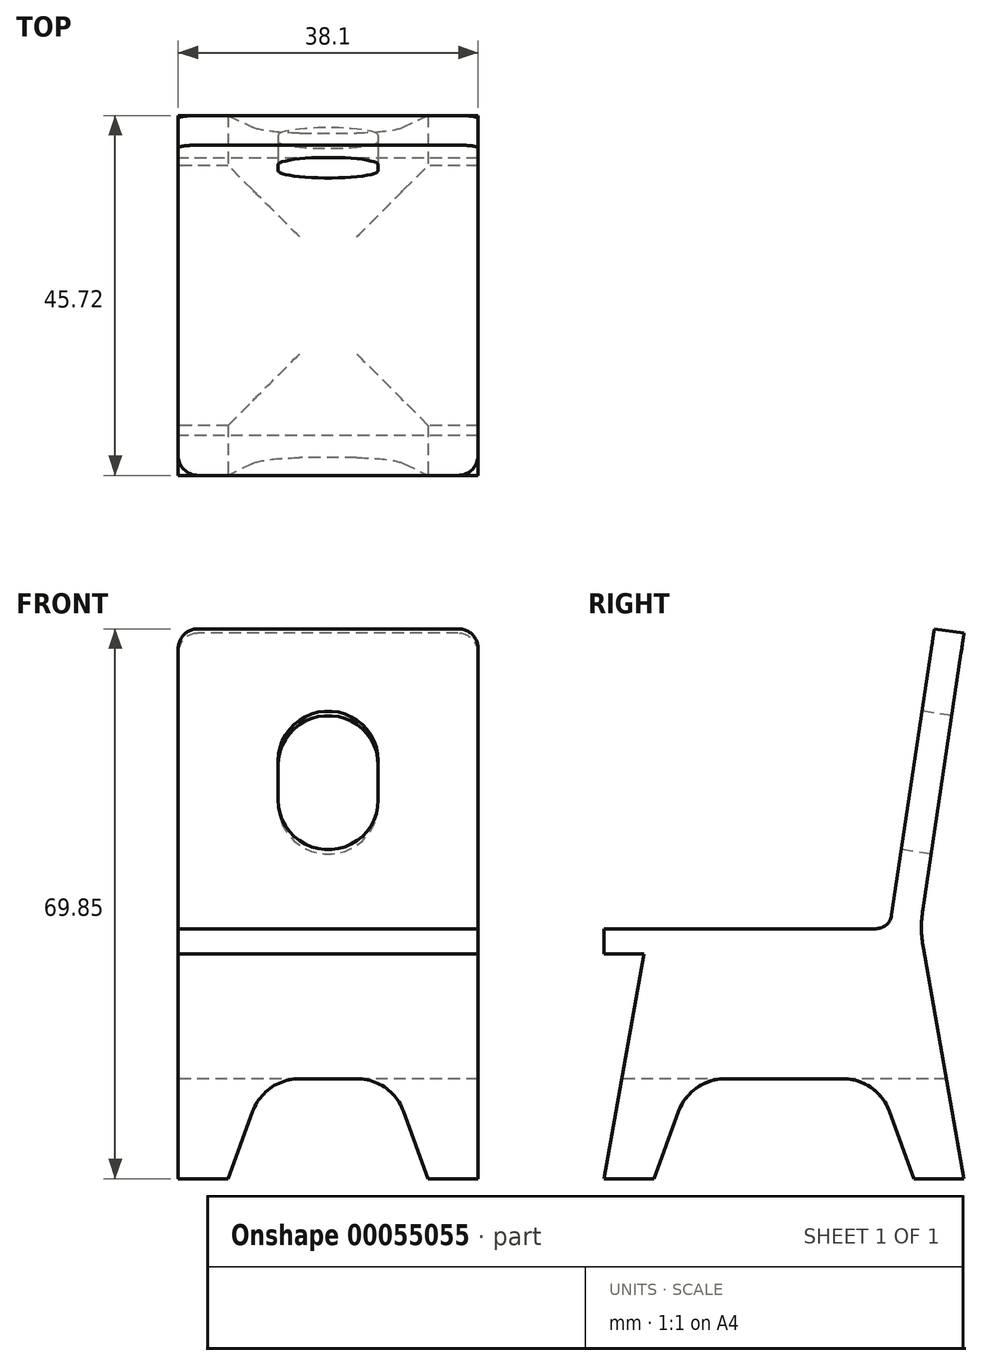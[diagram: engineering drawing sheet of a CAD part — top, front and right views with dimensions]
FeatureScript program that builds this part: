
annotation { "Feature Type Name" : "Feature", "Feature Type Description" : "" }
export const myFeature = defineFeature(function(context is Context, id is Id, definition is map)
    precondition{}
    {
        {
            var Q0;
            Q0=qCreatedBy(makeId("Right.planeOp"),FACE);
            var sketch = newSketch(context, id + "F0", { "sketchPlane" : qUnion([Q0])});
            skLineSegment(sketch, "E0", {"start": v(0.37, 2.45) * mm, "end": v(5.6, 37.54) * mm});
            skLineSegment(sketch, "E1", {"start": v(5.6, 37.54) * mm, "end": v(1.83, 38.1) * mm});
            skLineSegment(sketch, "E2", {"start": v(1.83, 38.1) * mm, "end": v(-3.6, 1.73) * mm});
            skLineSegment(sketch, "E3", {"start": v(-5.6, 0) * mm, "end": v(-40.12, 0) * mm});
            skLineSegment(sketch, "E4", {"start": v(-40.12, 0) * mm, "end": v(-40.12, -3.18) * mm});
            skLineSegment(sketch, "E5", {"start": v(-40.12, -3.18) * mm, "end": v(-35.08, -3.18) * mm});
            skLineSegment(sketch, "E6", {"start": v(-35.08, -3.18) * mm, "end": v(-40.12, -31.75) * mm});
            skLineSegment(sketch, "E7", {"start": v(-40.12, -31.75) * mm, "end": v(-33.77, -31.75) * mm});
            skLineSegment(sketch, "E8", {"start": v(-33.77, -31.75) * mm, "end": v(-30.67, -23.23) * mm});
            skLineSegment(sketch, "E9", {"start": v(-24.7, -19.05) * mm, "end": v(-9.82, -19.05) * mm});
            skLineSegment(sketch, "E10", {"start": v(-3.85, -23.23) * mm, "end": v(-0.75, -31.75) * mm});
            skLineSegment(sketch, "E11", {"start": v(5.6, -31.75) * mm, "end": v(0.43, -2.44) * mm});
            skLineSegment(sketch, "E12", {"start": v(-3.85, 0) * mm, "end": v(-3.85, 44.6) * mm, "construction": true});
            skLineSegment(sketch, "E13", {"start": v(-40.12, -3.18) * mm, "end": v(-40.12, -31.75) * mm, "construction": true});
            skLineSegment(sketch, "E14", {"start": v(-0.75, -31.75) * mm, "end": v(5.6, -31.75) * mm});
            skLineSegment(sketch, "E15", {"start": v(-33.77, -31.75) * mm, "end": v(-0.75, -31.75) * mm, "construction": true});
            skLineSegment(sketch, "E16", {"start": v(5.6, 37.54) * mm, "end": v(5.6, -31.75) * mm, "construction": true});
            skPoint(sketch, "E17.visualSharp", {"position": v(0, 0) * mm});
            skArc(sketch, "E17.filletArc", {"start": v(0.37, 2.45) * mm, "mid": v(0.2, 0) * mm, "end": v(0.43, -2.44) * mm});
            skPoint(sketch, "E18.visualSharp", {"position": v(-29.15, -19.05) * mm});
            skArc(sketch, "E18.filletArc", {"start": v(-24.7, -19.05) * mm, "mid": v(-28.35, -20.2) * mm, "end": v(-30.67, -23.23) * mm});
            skPoint(sketch, "E19.visualSharp", {"position": v(-5.37, -19.05) * mm});
            skArc(sketch, "E19.filletArc", {"start": v(-3.85, -23.23) * mm, "mid": v(-6.18, -20.2) * mm, "end": v(-9.82, -19.05) * mm});
            skPoint(sketch, "E20.visualSharp", {"position": v(-3.85, 0) * mm});
            skArc(sketch, "E20.filletArc", {"start": v(-5.6, 0) * mm, "mid": v(-4.28, 0.5) * mm, "end": v(-3.6, 1.73) * mm});
            skSolve(sketch);
        }
        {
            var Q0;
            Q0 = qSketchRegion(id + "F0", true);
            extrude(context, id + "F1", {"entities" : qUnion([Q0]), "endBound" : BoundingType.SYMMETRIC, "depth" : 38.1 * mm});
        }
        {
            var Q0;
            Q0=qCreatedBy(makeId("Front.planeOp"),FACE);
            var sketch = newSketch(context, id + "F2", { "sketchPlane" : qUnion([Q0])});
            skLineSegment(sketch, "E21", {"start": v(-12.7, -31.75) * mm, "end": v(-9.6, -23.23) * mm});
            skLineSegment(sketch, "E22", {"start": v(-3.63, -19.05) * mm, "end": v(0, -19.05) * mm});
            skLineSegment(sketch, "E23", {"start": v(0, -19.05) * mm, "end": v(0, -31.75) * mm, "construction": true});
            skLineSegment(sketch, "E24", {"start": v(0, -31.75) * mm, "end": v(-12.7, -31.75) * mm});
            skLineSegment(sketch, "E25.MirrorCS", {"start": v(0, -31.75) * mm, "end": v(12.7, -31.75) * mm});
            skLineSegment(sketch, "E26.MirrorCS", {"start": v(3.63, -19.05) * mm, "end": v(0, -19.05) * mm});
            skLineSegment(sketch, "E27.MirrorCS", {"start": v(12.7, -31.75) * mm, "end": v(9.6, -23.23) * mm});
            skPoint(sketch, "E28.visualSharp", {"position": v(-8.08, -19.05) * mm});
            skArc(sketch, "E28.filletArc", {"start": v(-3.63, -19.05) * mm, "mid": v(-7.27, -20.2) * mm, "end": v(-9.6, -23.23) * mm});
            skPoint(sketch, "E29.visualSharp", {"position": v(8.08, -19.05) * mm});
            skArc(sketch, "E29.filletArc", {"start": v(9.6, -23.23) * mm, "mid": v(7.27, -20.2) * mm, "end": v(3.63, -19.05) * mm});
            skSolve(sketch);
        }
        {
            var Q0;
            Q0 = qSketchRegion(id + "F2", true);
            extrude(context, id + "F3", {"entities" : qUnion([Q0]), "operationType" : NewBodyOperationType.REMOVE, "endBound" : BoundingType.THROUGH_ALL, "oppositeDirection" : true, "depth" : 25.4 * mm, "hasSecondDirection" : true, "secondDirectionBound" : SecondDirectionBoundingType.THROUGH_ALL, "secondDirectionOppositeDirection" : false, "secondDirectionDepth" : 25.4 * mm});
        }
        {
            var Q0;
            Q0=makeQuery(id+"F1.opExtrude","SWEPT_FACE",FACE,{"disambiguationData":[OSD([sQuery(id+"F0.wireOp",EDGE,"E2")])]});
            var sketch = newSketch(context, id + "F4", { "sketchPlane" : qUnion([Q0])});
            skLineSegment(sketch, "E30.rect.bottom", {"start": v(0, 27.37) * mm, "end": v(0, 27.37) * mm});
            skLineSegment(sketch, "E30.rect.top", {"start": v(0, 9.6) * mm, "end": v(0, 9.6) * mm});
            skLineSegment(sketch, "E30.rect.left", {"start": v(-6.35, 21.02) * mm, "end": v(-6.35, 15.94) * mm});
            skLineSegment(sketch, "E30.rect.right", {"start": v(6.35, 21.02) * mm, "end": v(6.35, 15.94) * mm});
            skPoint(sketch, "E30.rect.middle", {"position": v(0, 18.48) * mm});
            skPoint(sketch, "E31.visualSharp", {"position": v(-6.35, 27.37) * mm});
            skArc(sketch, "E31.filletArc", {"start": v(0, 27.37) * mm, "mid": v(-4.5, 25.51) * mm, "end": v(-6.35, 21.02) * mm});
            skPoint(sketch, "E32.visualSharp", {"position": v(6.35, 27.37) * mm});
            skArc(sketch, "E32.filletArc", {"start": v(6.35, 21.02) * mm, "mid": v(4.5, 25.51) * mm, "end": v(0, 27.37) * mm});
            skPoint(sketch, "E33.visualSharp", {"position": v(6.35, 9.6) * mm});
            skArc(sketch, "E33.filletArc", {"start": v(0, 9.6) * mm, "mid": v(4.5, 11.45) * mm, "end": v(6.35, 15.94) * mm});
            skPoint(sketch, "E34.visualSharp", {"position": v(-6.35, 9.6) * mm});
            skArc(sketch, "E34.filletArc", {"start": v(-6.35, 15.94) * mm, "mid": v(-4.5, 11.45) * mm, "end": v(0, 9.6) * mm});
            skSolve(sketch);
        }
        {
            var Q0;
            Q0 = qSketchRegion(id + "F4", true);
            extrude(context, id + "F5", {"entities" : qUnion([Q0]), "operationType" : NewBodyOperationType.REMOVE, "endBound" : BoundingType.THROUGH_ALL, "oppositeDirection" : true, "depth" : 25.4 * mm});
        }
        {
            var Q0;
            Q0=makeQuery(id+"F1.opExtrude","CAP_EDGE",EDGE,{"disambiguationData":[OSD([sQuery(id+"F0.wireOp",EDGE,"E1")])],"isStart":false});
            var Q1;
            Q1=makeQuery(id+"F1.opExtrude","CAP_EDGE",EDGE,{"disambiguationData":[OSD([sQuery(id+"F0.wireOp",EDGE,"E1")])],"isStart":true});
            var Q2;
            Q2=makeQuery(id+"F1.opExtrude","CAP_EDGE",EDGE,{"disambiguationData":[OSD([sQuery(id+"F0.wireOp",EDGE,"E4")])],"isStart":true});
            var Q3;
            Q3=makeQuery(id+"F1.opExtrude","CAP_EDGE",EDGE,{"disambiguationData":[OSD([sQuery(id+"F0.wireOp",EDGE,"E4")])],"isStart":false});
            fillet(context, id + "F6", {"entities" : qUnion([Q0, Q1, Q2, Q3]), "radius" : 2.54 * mm, "tangentPropagation" : true, "allowEdgeOverflow" : false});
        }
    });
